# Revit family: PRD_FrankeWS_WshbsnTps_ExtensionAdapterForF3EBibTap_ACEV1001
name_source: partatom
category: Specialty Equipment
revit_build: Autodesk Revit 2018 (Build: 20190510_1515(x64)
units: mm (PartAtom-declared; Revit-internal decimal feet)

## family parameters
Always vertical = No
Cut with Voids When Loaded = No
OmniClass Number = 23.45.05.14.99
OmniClass Title = Other Sanitary Washing Plumbing Fixtures
Part Type = Normal
Room Calculation Point = No
Round Connector Dimension = Use Diameter
Shared = No
Work Plane-Based = Yes

## types (1)
- ACEV1001
    AssetType = Fixed
    BIMObjectName = PRD_AR_WashbasinTaps_ExtensionAdapterForF3EBibTap_ACEV1001
    BodyMaterial = PRD_AR_ChromatedBrass_HighPolished
    Category = Pr_40_20_87_98, Washbasin taps
    Default Elevation = 1219 mm
    Description = Extension adapter for F3E bib tap, 30 mm, maximum 1-times stackable, polished chromium-plated brass.
    DurationUnit = year
    Features = polished chromium-plated brass
    Finish = polished chromium-plated
    GrossWeight = 0.45 kg
    IfcExportAs = IfcSanitaryTerminalType
    IfcExportType = USERDEFINED
    Manufacturer = KWC Group AG
    ManufacturerName = KWC Group AG
    ManufacturerURL = www.kwc.com
    Material = Brass
    Model = ACEV1001
    ModelNumber = 2030043823
    ModelReference = ACEV1001
    NBSDescription = Water supply fittings for wash basins and troughs
    NBSReference = 45-35-70/371
    Name = Extension adapter for F3E bib tap ACEV1001
    NetWeight = 0.40 kg
    NominalDepth = 0 mm  [stored 0 ft]
    NominalHeight = 0 mm  [stored 0 ft]
    NominalLength = 0 mm  [stored 0 ft]
    NominalWidth = 0 mm  [stored 0 ft]
    ProductCode = 208.0637.697
    ProductInformation = https://pim.kwc.com
    Status = New
    TailorMade = No
    TypeOfExtension = For bib taps
    URL = www.kwc.com
    Uniclass2015Code = Pr_40_20_87_98
    Uniclass2015Title = Washbasin taps
    Uniclass2015Version = Products v1.23
    Version = 1
    WarrantyDurationUnit = year

note: [stored X ft] marks values corroborated as IEEE doubles in the binary element streams (Revit-internal decimal feet)

## geometry (parser evidence)
native form markers: Sweep x3
no freeform markers — native parametric forms only
